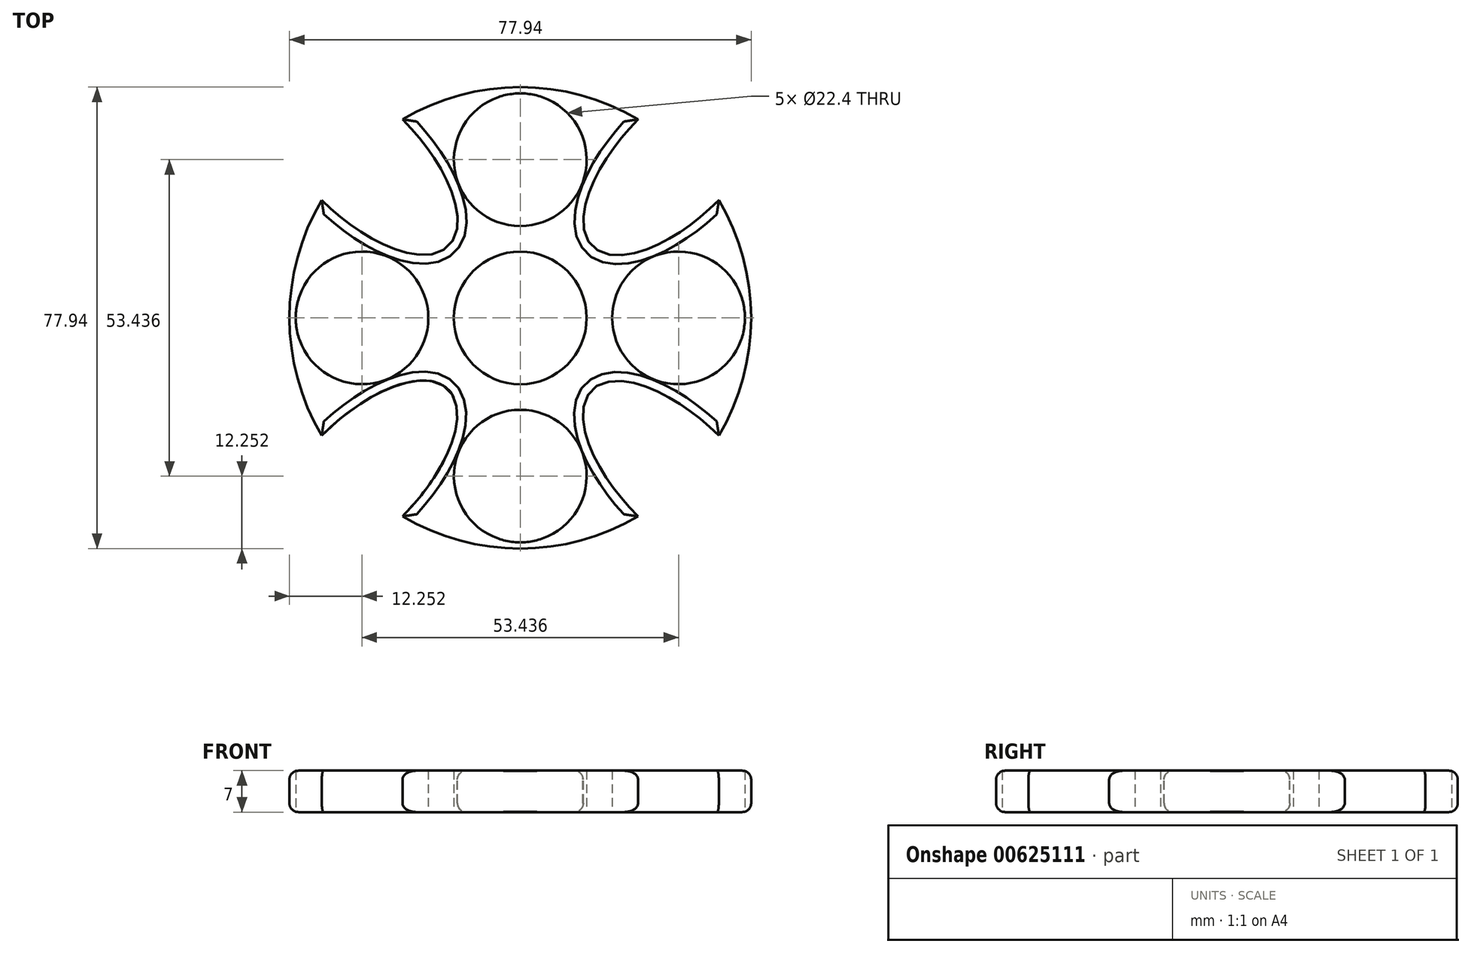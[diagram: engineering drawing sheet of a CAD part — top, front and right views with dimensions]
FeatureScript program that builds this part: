
annotation { "Feature Type Name" : "Feature", "Feature Type Description" : "" }
export const myFeature = defineFeature(function(context is Context, id is Id, definition is map)
    precondition{}
    {
        {
            var Q0;
            Q0=qCreatedBy(makeId("Top.planeOp"),FACE);
            var sketch = newSketch(context, id + "F0", { "sketchPlane" : qUnion([Q0])});
            skCircle(sketch, "E0", {"center": v(0, 0) * mm, "radius": 11.2 * mm});
            skCircle(sketch, "E1", {"center": v(0, 26.72) * mm, "radius": 11.2 * mm});
            skCircle(sketch, "E2.1.0", {"center": v(-26.72, 0) * mm, "radius": 11.2 * mm});
            skCircle(sketch, "E2.2.0", {"center": v(0, -26.72) * mm, "radius": 11.2 * mm});
            skCircle(sketch, "E2.3.0", {"center": v(26.72, 0) * mm, "radius": 11.2 * mm});
            skPoint(sketch, "E3.trimOffspring.end.orphan", {"position": v(0, 39.92) * mm});
            skPoint(sketch, "E2.3.1.start.orphan", {"position": v(39.92, 0) * mm});
            skArc(sketch, "E4", {"start": v(19.89, 33.51) * mm, "mid": v(0, 38.97) * mm, "end": v(-19.89, 33.51) * mm});
            skEllipticalArc(sketch, "E5", {});
            skEllipticalArc(sketch, "E6.1.0", {});
            skEllipticalArc(sketch, "E6.2.0", {});
            skEllipticalArc(sketch, "E6.3.0", {});
            skArc(sketch, "E7.trimOffspring", {"start": v(-33.51, 19.89) * mm, "mid": v(-38.97, 0) * mm, "end": v(-33.51, -19.89) * mm});
            skArc(sketch, "E8.trimOffspring", {"start": v(-19.89, -33.51) * mm, "mid": v(0, -38.97) * mm, "end": v(19.89, -33.51) * mm});
            skArc(sketch, "E9.trimOffspring", {"start": v(33.51, -19.89) * mm, "mid": v(38.97, 0) * mm, "end": v(33.51, 19.89) * mm});
            const initialGuessF0  = {"E5": [0.026718035340309233, 0.026718035340309094, -0.704661751514044, -0.7095433855326677, 0.020634290755595388, 0.009633863948574824, 4.711920405036167, 1.5680400813385], "E6.1.0": [-0.026718035340309098, 0.02671803534030923, 0.7095433855326677, -0.704661751514044, 0.020634290755595388, 0.009633863948574824, 4.711920405036167, 1.5680400813384998], "E6.2.0": [-0.026718035340309233, -0.026718035340309094, 0.704661751514044, 0.7095433855326677, 0.020634290755595388, 0.009633863948574824, 4.711920405036167, 1.5680400813385], "E6.3.0": [0.026718035340309094, -0.026718035340309233, -0.7095433855326678, 0.7046617515140439, 0.020634290755595388, 0.009633863948574824, 4.711920405036167, 1.5680400813385]};
            skSetInitialGuess(sketch, initialGuessF0);
            skSolve(sketch);
        }
        {
            var Q0;
            Q0=makeQuery(id+"F0.imprint","IMPRINT",FACE,{"disambiguationData":[TD([[makeQuery(id+"F0.imprint","IMPRINT",EDGE,{"derivedFrom":sQuery(id+"F0.wireOp",EDGE,"E0")}),-1.0]])]});
            extrude(context, id + "F1", {"entities" : qUnion([Q0]), "depth" : 7 * mm, "offsetDistance" : 25 * mm});
        }
        {
            var Q0;
            Q0=makeQuery(id+"F1.opExtrude","CAP_EDGE",EDGE,{"disambiguationData":[OSD([sQuery(id+"F0.wireOp",EDGE,"E6.1.0")])],"isStart":false});
            var Q1;
            Q1=makeQuery(id+"F1.opExtrude","CAP_EDGE",EDGE,{"disambiguationData":[OSD([sQuery(id+"F0.wireOp",EDGE,"E4")])],"isStart":false});
            var Q2;
            Q2=makeQuery(id+"F1.opExtrude","CAP_EDGE",EDGE,{"disambiguationData":[OSD([sQuery(id+"F0.wireOp",EDGE,"E9.trimOffspring")])],"isStart":false});
            var Q3;
            Q3=makeQuery(id+"F1.opExtrude","CAP_EDGE",EDGE,{"disambiguationData":[OSD([sQuery(id+"F0.wireOp",EDGE,"E5")])],"isStart":false});
            var Q4;
            Q4=makeQuery(id+"F1.opExtrude","CAP_EDGE",EDGE,{"disambiguationData":[OSD([sQuery(id+"F0.wireOp",EDGE,"E6.3.0")])],"isStart":false});
            var Q5;
            Q5=makeQuery(id+"F1.opExtrude","CAP_EDGE",EDGE,{"disambiguationData":[OSD([sQuery(id+"F0.wireOp",EDGE,"E8.trimOffspring")])],"isStart":false});
            var Q6;
            Q6=makeQuery(id+"F1.opExtrude","CAP_EDGE",EDGE,{"disambiguationData":[OSD([sQuery(id+"F0.wireOp",EDGE,"E6.2.0")])],"isStart":false});
            var Q7;
            Q7=makeQuery(id+"F1.opExtrude","CAP_EDGE",EDGE,{"disambiguationData":[OSD([sQuery(id+"F0.wireOp",EDGE,"E7.trimOffspring")])],"isStart":false});
            fillet(context, id + "F2", {"entities" : qUnion([Q0, Q1, Q2, Q3, Q4, Q5, Q6, Q7]), "radius" : 1.5 * mm, "tangentPropagation" : true, "allowEdgeOverflow" : false});
        }
        {
            var Q0;
            Q0=makeQuery(id+"F1.opExtrude","CAP_EDGE",EDGE,{"disambiguationData":[OSD([sQuery(id+"F0.wireOp",EDGE,"E8.trimOffspring")])],"isStart":true});
            var Q1;
            Q1=makeQuery(id+"F1.opExtrude","CAP_EDGE",EDGE,{"disambiguationData":[OSD([sQuery(id+"F0.wireOp",EDGE,"E6.2.0")])],"isStart":true});
            var Q2;
            Q2=makeQuery(id+"F1.opExtrude","CAP_EDGE",EDGE,{"disambiguationData":[OSD([sQuery(id+"F0.wireOp",EDGE,"E7.trimOffspring")])],"isStart":true});
            var Q3;
            Q3=makeQuery(id+"F1.opExtrude","CAP_EDGE",EDGE,{"disambiguationData":[OSD([sQuery(id+"F0.wireOp",EDGE,"E6.1.0")])],"isStart":true});
            var Q4;
            Q4=makeQuery(id+"F1.opExtrude","CAP_EDGE",EDGE,{"disambiguationData":[OSD([sQuery(id+"F0.wireOp",EDGE,"E4")])],"isStart":true});
            var Q5;
            Q5=makeQuery(id+"F1.opExtrude","CAP_EDGE",EDGE,{"disambiguationData":[OSD([sQuery(id+"F0.wireOp",EDGE,"E5")])],"isStart":true});
            var Q6;
            Q6=makeQuery(id+"F1.opExtrude","CAP_EDGE",EDGE,{"disambiguationData":[OSD([sQuery(id+"F0.wireOp",EDGE,"E6.3.0")])],"isStart":true});
            var Q7;
            Q7=makeQuery(id+"F1.opExtrude","CAP_EDGE",EDGE,{"disambiguationData":[OSD([sQuery(id+"F0.wireOp",EDGE,"E9.trimOffspring")])],"isStart":true});
            fillet(context, id + "F3", {"entities" : qUnion([Q0, Q1, Q2, Q3, Q4, Q5, Q6, Q7]), "radius" : 1.5 * mm, "tangentPropagation" : true, "allowEdgeOverflow" : false});
        }
    });
